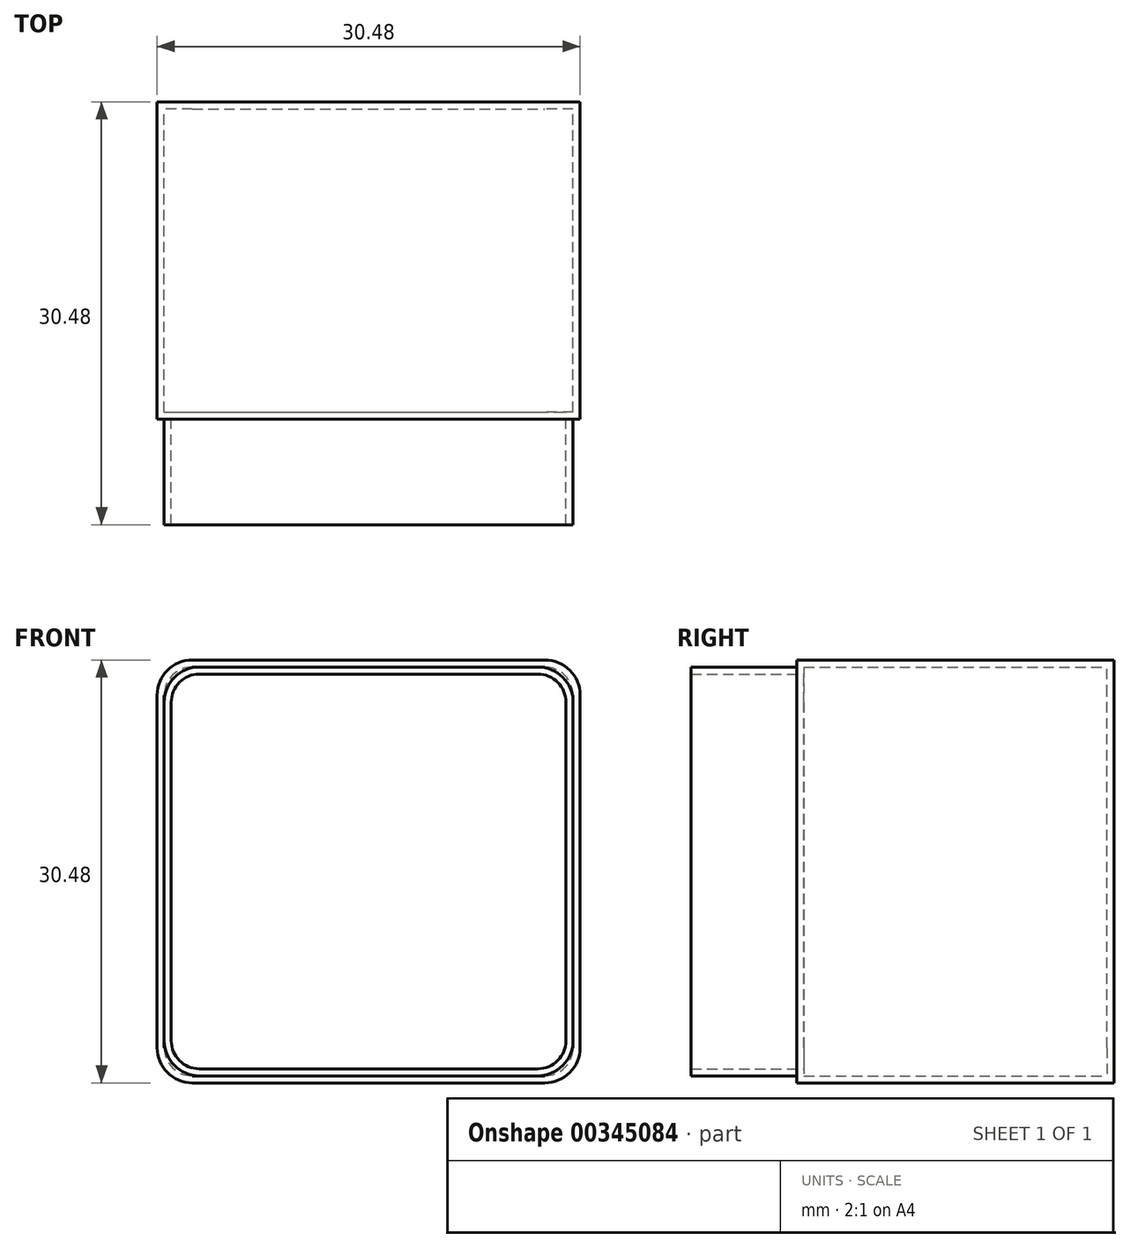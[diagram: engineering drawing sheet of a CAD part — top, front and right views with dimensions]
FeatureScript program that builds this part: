
annotation { "Feature Type Name" : "Feature", "Feature Type Description" : "" }
export const myFeature = defineFeature(function(context is Context, id is Id, definition is map)
    precondition{}
    {
        {
            var Q0;
            Q0=qCreatedBy(makeId("Front.planeOp"),FACE);
            var sketch = newSketch(context, id + "F0", { "sketchPlane" : qUnion([Q0])});
            skLineSegment(sketch, "E0.bottom", {"start": v(0, 0) * mm, "end": v(30.48, 0) * mm});
            skLineSegment(sketch, "E0.top", {"start": v(0, 30.48) * mm, "end": v(30.48, 30.48) * mm});
            skLineSegment(sketch, "E0.left", {"start": v(0, 0) * mm, "end": v(0, 30.48) * mm});
            skLineSegment(sketch, "E0.right", {"start": v(30.48, 0) * mm, "end": v(30.48, 30.48) * mm});
            skSolve(sketch);
        }
        {
            var Q0;
            Q0=makeQuery(id+"F0.imprint","IMPRINT",FACE,{"disambiguationData":[TD([[makeQuery(id+"F0.imprint","IMPRINT",EDGE,{"derivedFrom":sQuery(id+"F0.wireOp",EDGE,"E0.bottom")}),1.0]])]});
            extrude(context, id + "F1", {"entities" : qUnion([Q0]), "depth" : 22.86 * mm});
        }
        {
            var Q0;
            Q0=makeQuery(id+"F1.opExtrude","CAP_FACE",FACE,{"disambiguationData":[OSD([sQuery(id+"F0.wireOp",EDGE,"E0.bottom"),sQuery(id+"F0.wireOp",EDGE,"E0.top"),sQuery(id+"F0.wireOp",EDGE,"E0.left"),sQuery(id+"F0.wireOp",EDGE,"E0.right")])],"isStart":false});
            var sketch = newSketch(context, id + "F2", { "sketchPlane" : qUnion([Q0])});
            skLineSegment(sketch, "E1.bottom", {"start": v(0.5, 29.97) * mm, "end": v(29.97, 29.97) * mm});
            skLineSegment(sketch, "E1.top", {"start": v(0.5, 0.5) * mm, "end": v(29.97, 0.5) * mm});
            skLineSegment(sketch, "E1.left", {"start": v(0.5, 29.97) * mm, "end": v(0.5, 0.5) * mm});
            skLineSegment(sketch, "E1.right", {"start": v(29.97, 29.97) * mm, "end": v(29.97, 0.5) * mm});
            skSolve(sketch);
        }
        {
            var Q0;
            Q0=makeQuery(id+"F2.imprint","IMPRINT",FACE,{"disambiguationData":[TD([[makeQuery(id+"F2.imprint","IMPRINT",EDGE,{"derivedFrom":sQuery(id+"F2.wireOp",EDGE,"E1.bottom")}),-1.0]])]});
            extrude(context, id + "F3", {"entities" : qUnion([Q0]), "operationType" : NewBodyOperationType.ADD, "depth" : 7.62 * mm});
        }
        {
            var Q0;
            Q0=makeQuery(id+"F1.opExtrude","SWEPT_EDGE",EDGE,{"disambiguationData":[OSD([sQuery(id+"F0.wireOp",EDGE,"E0.top"),sQuery(id+"F0.wireOp",EDGE,"E0.right")])]});
            var Q1;
            Q1=makeQuery(id+"F3.opExtrude","SWEPT_EDGE",EDGE,{"disambiguationData":[OSD([sQuery(id+"F2.wireOp",EDGE,"E1.bottom"),sQuery(id+"F2.wireOp",EDGE,"E1.right")])]});
            var Q2;
            Q2=makeQuery(id+"F3.opExtrude","SWEPT_EDGE",EDGE,{"disambiguationData":[OSD([sQuery(id+"F2.wireOp",EDGE,"E1.bottom"),sQuery(id+"F2.wireOp",EDGE,"E1.left")])]});
            var Q3;
            Q3=makeQuery(id+"F1.opExtrude","SWEPT_EDGE",EDGE,{"disambiguationData":[OSD([sQuery(id+"F0.wireOp",EDGE,"E0.top"),sQuery(id+"F0.wireOp",EDGE,"E0.left")])]});
            var Q4;
            Q4=makeQuery(id+"F1.opExtrude","SWEPT_EDGE",EDGE,{"disambiguationData":[OSD([sQuery(id+"F0.wireOp",EDGE,"E0.bottom"),sQuery(id+"F0.wireOp",EDGE,"E0.left")])]});
            var Q5;
            Q5=makeQuery(id+"F3.opExtrude","SWEPT_EDGE",EDGE,{"disambiguationData":[OSD([sQuery(id+"F2.wireOp",EDGE,"E1.top"),sQuery(id+"F2.wireOp",EDGE,"E1.left")])]});
            var Q6;
            Q6=makeQuery(id+"F1.opExtrude","SWEPT_EDGE",EDGE,{"disambiguationData":[OSD([sQuery(id+"F0.wireOp",EDGE,"E0.bottom"),sQuery(id+"F0.wireOp",EDGE,"E0.right")])]});
            var Q7;
            Q7=makeQuery(id+"F3.opExtrude","SWEPT_EDGE",EDGE,{"disambiguationData":[OSD([sQuery(id+"F2.wireOp",EDGE,"E1.top"),sQuery(id+"F2.wireOp",EDGE,"E1.right")])]});
            fillet(context, id + "F4", {"entities" : qUnion([Q0, Q1, Q2, Q3, Q4, Q5, Q6, Q7]), "radius" : 2.54 * mm, "tangentPropagation" : true, "allowEdgeOverflow" : false});
        }
        {
            var Q0;
            Q0=makeQuery(id+"F3.opExtrude","CAP_FACE",FACE,{"disambiguationData":[OSD([sQuery(id+"F2.wireOp",EDGE,"E1.bottom"),sQuery(id+"F2.wireOp",EDGE,"E1.top"),sQuery(id+"F2.wireOp",EDGE,"E1.left"),sQuery(id+"F2.wireOp",EDGE,"E1.right")])],"isStart":false});
            shell(context, id + "F5", {"entities" : qUnion([Q0]), "thickness" : 0.5 * mm});
        }
    });
